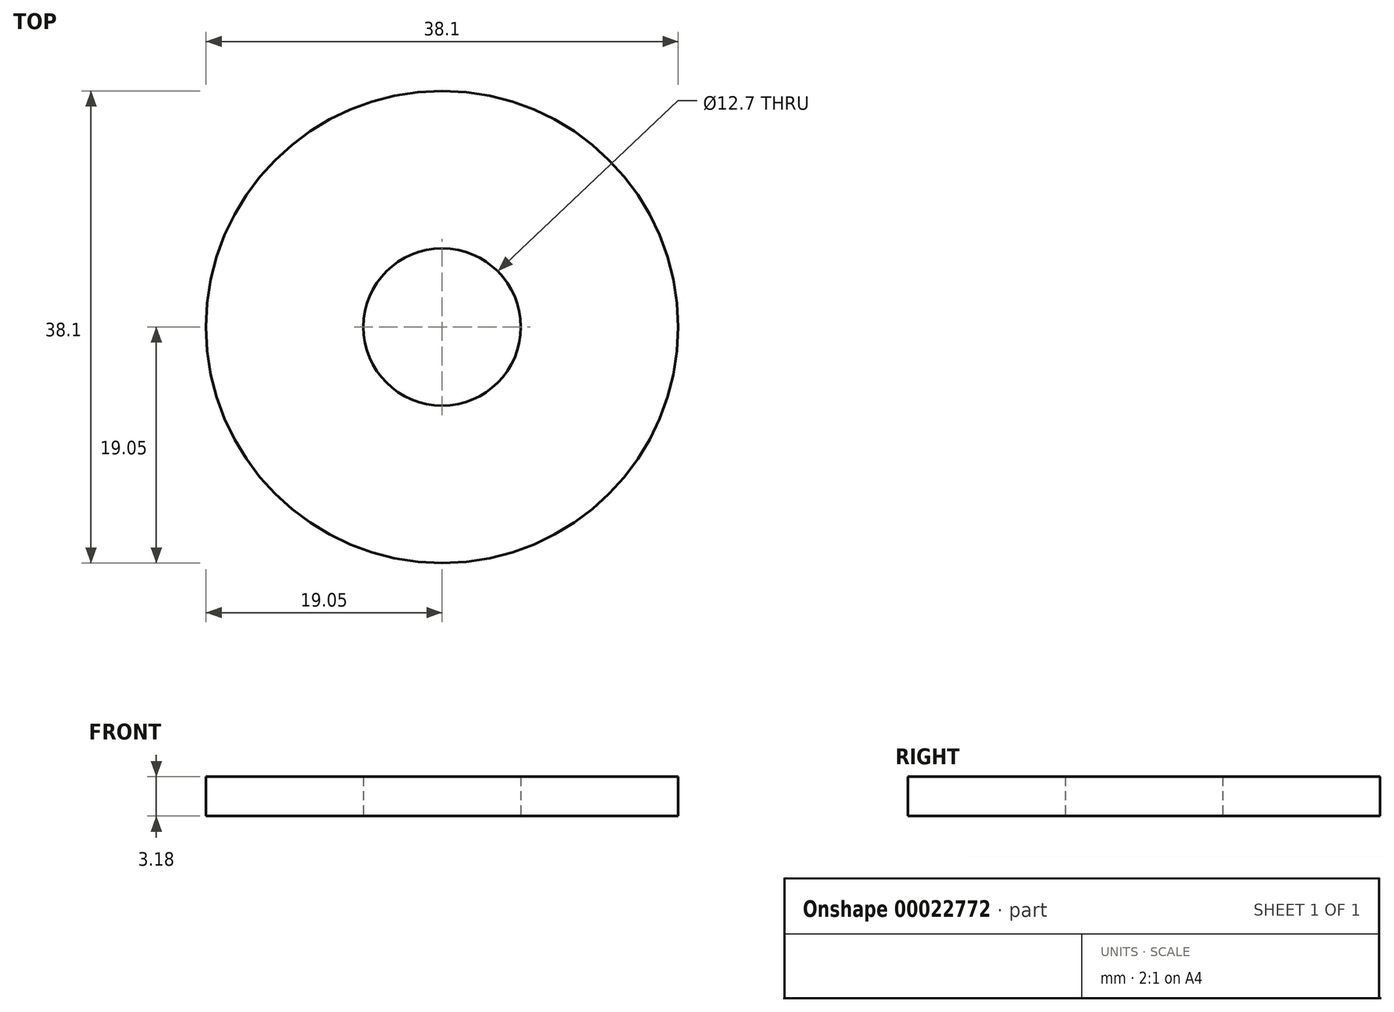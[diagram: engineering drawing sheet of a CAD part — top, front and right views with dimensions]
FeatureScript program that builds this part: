
annotation { "Feature Type Name" : "Feature", "Feature Type Description" : "" }
export const myFeature = defineFeature(function(context is Context, id is Id, definition is map)
    precondition{}
    {
        {
            var Q0;
            Q0=qCreatedBy(makeId("Top.planeOp"),FACE);
            var sketch = newSketch(context, id + "F0", { "sketchPlane" : qUnion([Q0])});
            skCircle(sketch, "E0", {"center": v(0, 0) * mm, "radius": 19.05 * mm});
            skSolve(sketch);
        }
        {
            var Q0;
            Q0 = qSketchRegion(id + "F0", true);
            extrude(context, id + "F1", {"entities" : qUnion([Q0]), "depth" : 3.17 * mm});
        }
        {
            var Q0;
            Q0=makeQuery(id+"F1.opExtrude","CAP_FACE",FACE,{"disambiguationData":[OSD([sQuery(id+"F0.wireOp",EDGE,"E0")])],"isStart":true});
            var sketch = newSketch(context, id + "F2", { "sketchPlane" : qUnion([Q0])});
            skCircle(sketch, "E1", {"center": v(0, 0) * mm, "radius": 6.35 * mm});
            skSolve(sketch);
        }
        {
            var Q0;
            Q0 = qSketchRegion(id + "F2", true);
            extrude(context, id + "F3", {"entities" : qUnion([Q0]), "operationType" : NewBodyOperationType.REMOVE, "endBound" : BoundingType.THROUGH_ALL, "oppositeDirection" : true, "depth" : 25.4 * mm});
        }
    });
